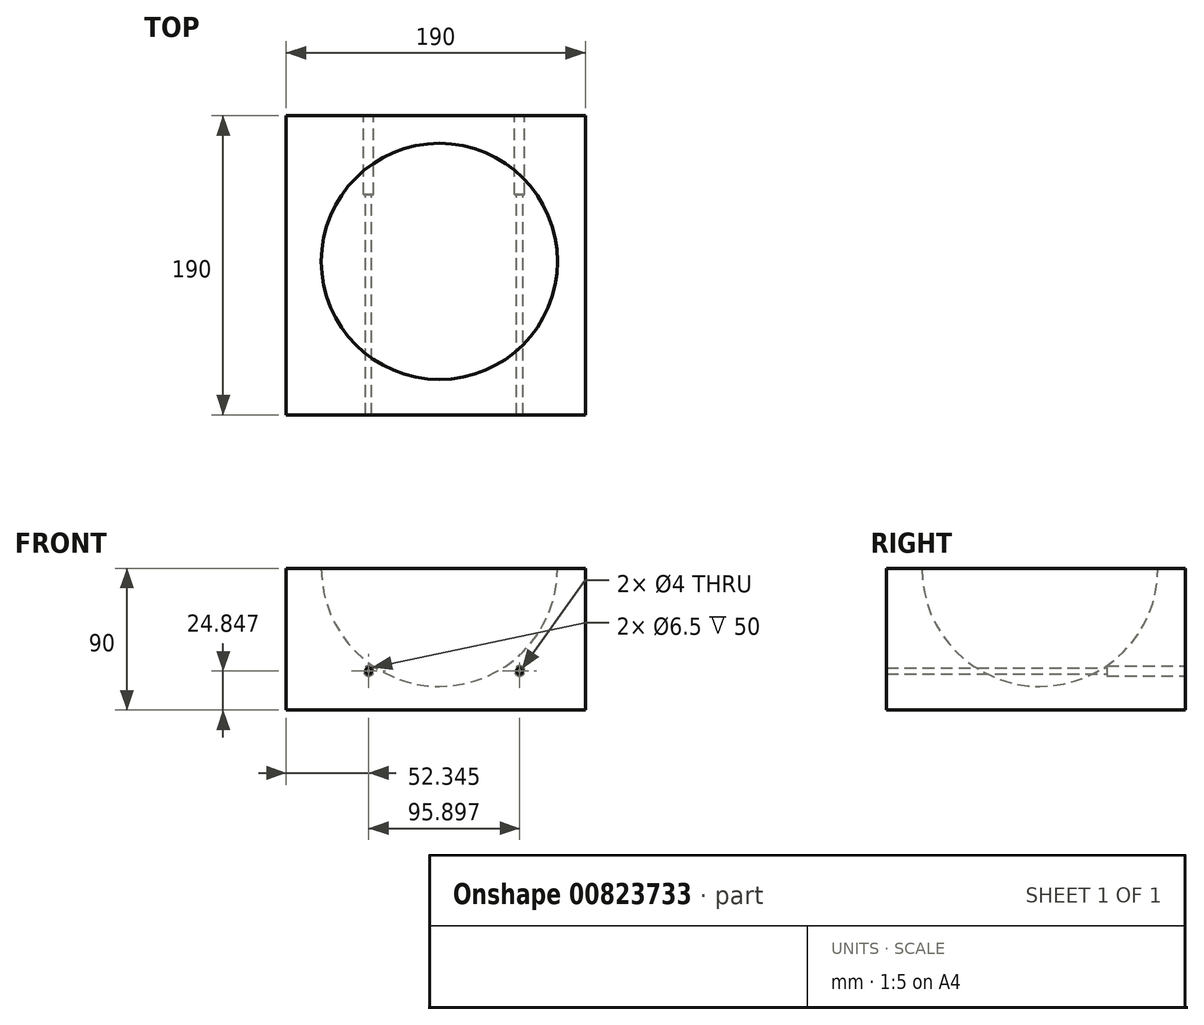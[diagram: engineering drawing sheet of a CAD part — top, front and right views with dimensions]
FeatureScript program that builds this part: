
annotation { "Feature Type Name" : "Feature", "Feature Type Description" : "" }
export const myFeature = defineFeature(function(context is Context, id is Id, definition is map)
    precondition{}
    {
        {
            var Q0;
            Q0=qCreatedBy(makeId("Top.planeOp"),FACE);
            var sketch = newSketch(context, id + "F0", { "sketchPlane" : qUnion([Q0])});
            skLineSegment(sketch, "E0.bottom", {"start": v(-97.28, 92.5) * mm, "end": v(92.72, 92.5) * mm});
            skLineSegment(sketch, "E0.top", {"start": v(-97.28, -97.5) * mm, "end": v(92.72, -97.5) * mm});
            skLineSegment(sketch, "E0.left", {"start": v(-97.28, 92.5) * mm, "end": v(-97.28, -97.5) * mm});
            skLineSegment(sketch, "E0.right", {"start": v(92.72, 92.5) * mm, "end": v(92.72, -97.5) * mm});
            skSolve(sketch);
        }
        {
            var Q0;
            Q0 = qSketchRegion(id + "F0", true);
            extrude(context, id + "F1", {"entities" : qUnion([Q0]), "depth" : 90 * mm, "offsetDistance" : 25 * mm});
        }
        {
            var Q0;
            Q0=makeQuery(id+"F1.opExtrude","CAP_FACE",FACE,{"disambiguationData":[OSD([sQuery(id+"F0.wireOp",EDGE,"E0.bottom"),sQuery(id+"F0.wireOp",EDGE,"E0.top"),sQuery(id+"F0.wireOp",EDGE,"E0.left"),sQuery(id+"F0.wireOp",EDGE,"E0.right")])],"isStart":false});
            var sketch = newSketch(context, id + "F2", { "sketchPlane" : qUnion([Q0])});
            skArc(sketch, "E1", {"start": v(-75, 0) * mm, "mid": v(0, -75) * mm, "end": v(75, 0) * mm});
            skPoint(sketch, "E2.startSnap0", {"position": v(-97.28, -2.5) * mm});
            skLineSegment(sketch, "E3", {"start": v(-75, 0) * mm, "end": v(75, 0) * mm});
            skSolve(sketch);
        }
        {
            var Q0;
            Q0=makeQuery(id+"F2.imprint","IMPRINT",FACE,{"disambiguationData":[TD([[makeQuery(id+"F2.imprint","IMPRINT",EDGE,{"derivedFrom":sQuery(id+"F2.wireOp",EDGE,"E1")}),1.0]])]});
            var Q1;
            Q1=sQuery(id+"F2.wireOp",EDGE,"E3");
            revolve(context, id + "F3", {"operationType" : NewBodyOperationType.REMOVE, "surfaceOperationType" : NewSurfaceOperationType.NEW, "entities" : qUnion([Q0]), "axis" : qUnion([Q1]), "revolveType" : RevolveType.FULL, "oppositeDirection" : true});
        }
        {
            var Q0;
            Q0=makeQuery(id+"F1.opExtrude","SWEPT_FACE",FACE,{"disambiguationData":[OSD([sQuery(id+"F0.wireOp",EDGE,"E0.bottom")])]});
            var sketch = newSketch(context, id + "F4", { "sketchPlane" : qUnion([Q0])});
            skPoint(sketch, "E4", {"position": v(44.94, 24.85) * mm});
            skPoint(sketch, "E5", {"position": v(-50.96, 24.85) * mm});
            skSolve(sketch);
        }
        {
            var Q0;
            Q0=sQuery(id+"F4.wireOp",VERTEX,"E4");
            var Q1;
            Q1=sQuery(id+"F4.wireOp",VERTEX,"E5");
            var Q2;
            Q2=makeQuery(id+"F1.opExtrude","SWEPT_BODY",BODY,{"disambiguationData":[OSD([sQuery(id+"F0.wireOp",EDGE,"E0.bottom"),sQuery(id+"F0.wireOp",EDGE,"E0.top"),sQuery(id+"F0.wireOp",EDGE,"E0.left"),sQuery(id+"F0.wireOp",EDGE,"E0.right")])]});
            hole(context, id + "F5", {"style" : HoleStyle.C_BORE, "endStyle" : HoleEndStyle.THROUGH, "holeDiameter" : 4 * mm, "cBoreDiameter" : 6.5 * mm, "cBoreDepth" : 50 * mm, "majorDiameter" : 5 * mm, "isTappedThrough" : true, "tappedDepth" : 12 * mm, "tapClearance" : 3, "startFromSketch" : true, "locations" : qUnion([Q0, Q1]), "scope" : qUnion([Q2])});
        }
    });
